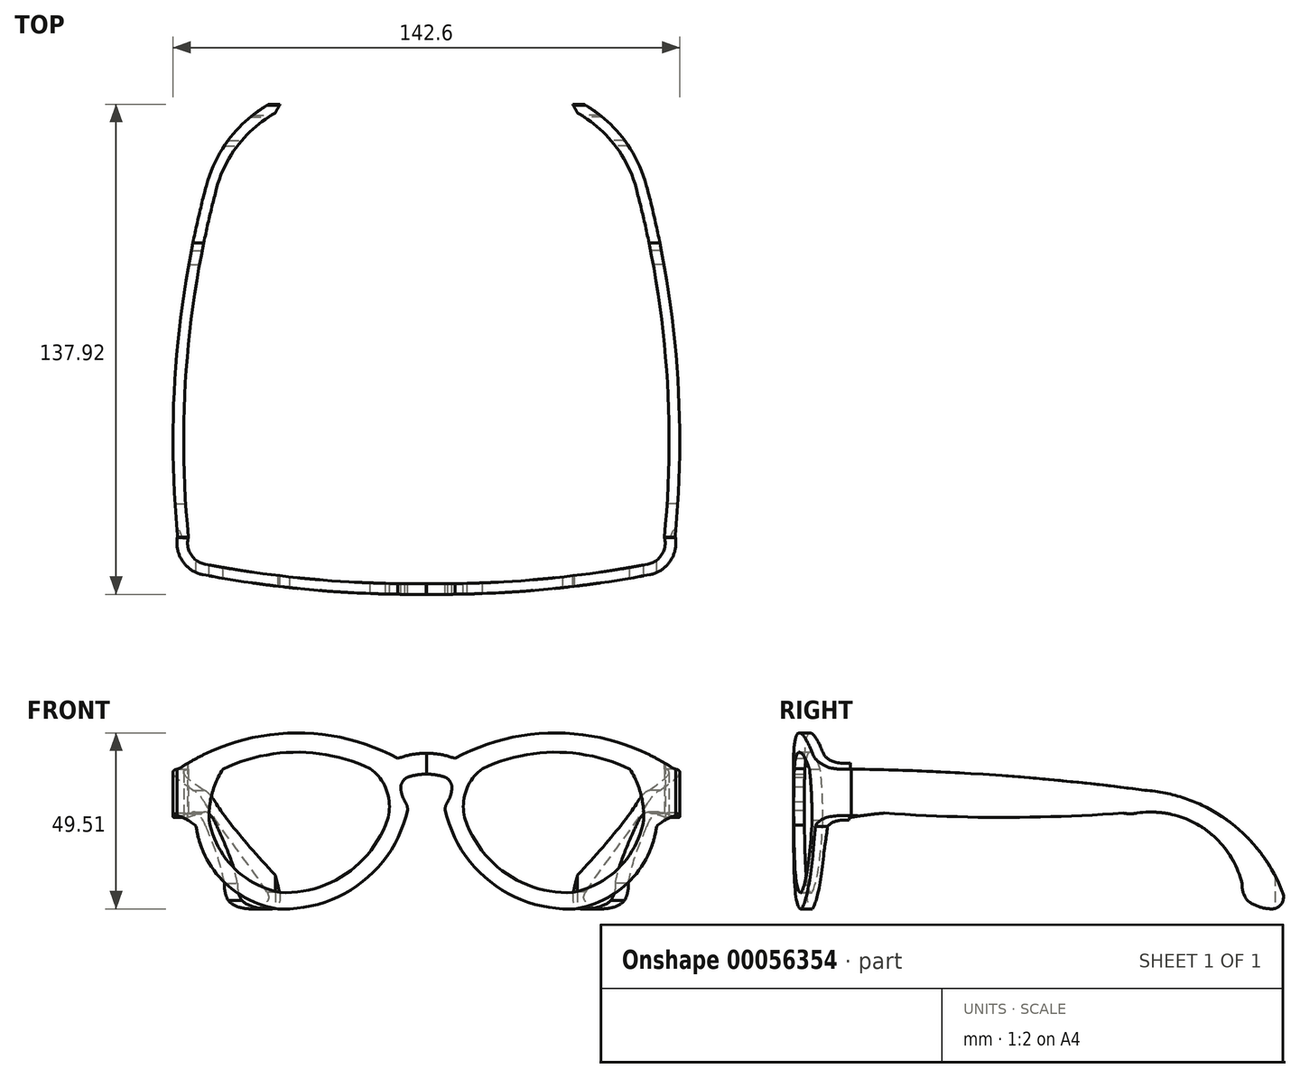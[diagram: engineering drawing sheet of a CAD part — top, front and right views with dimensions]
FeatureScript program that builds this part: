
annotation { "Feature Type Name" : "Feature", "Feature Type Description" : "" }
export const myFeature = defineFeature(function(context is Context, id is Id, definition is map)
    precondition{}
    {
        {
            var Q0;
            Q0=qCreatedBy(makeId("Top.planeOp"),FACE);
            var sketch = newSketch(context, id + "F0", { "sketchPlane" : qUnion([Q0])});
            skLineSegment(sketch, "E0.MirrorCS", {"start": v(42.53, 129.95) * mm, "end": v(40, 134.5) * mm});
            skArc(sketch, "E1.MirrorCS", {"start": v(66.96, 10.6) * mm, "mid": v(66.29, 5.73) * mm, "end": v(62.24, 2.95) * mm});
            skArc(sketch, "E2.MirrorCS", {"start": v(42.53, 129.95) * mm, "mid": v(52.96, 120.97) * mm, "end": v(59.06, 108.64) * mm});
            skArc(sketch, "E3.MirrorCS", {"start": v(62.8, 0) * mm, "mid": v(31.53, -4.3) * mm, "end": v(0, -5.5) * mm});
            skArc(sketch, "E4.MirrorCS", {"start": v(70, 10.8) * mm, "mid": v(68.67, 3.89) * mm, "end": v(62.8, 0) * mm});
            skArc(sketch, "E5.MirrorCS", {"start": v(61.96, 109.4) * mm, "mid": v(70.37, 60.47) * mm, "end": v(70, 10.8) * mm});
            skArc(sketch, "E6.MirrorCS", {"start": v(59.06, 108.64) * mm, "mid": v(67.4, 59.97) * mm, "end": v(66.96, 10.6) * mm});
            skArc(sketch, "E7.MirrorCS", {"start": v(40, 134.5) * mm, "mid": v(53.92, 124.52) * mm, "end": v(61.96, 109.4) * mm});
            skArc(sketch, "E8.MirrorCS", {"start": v(62.24, 2.95) * mm, "mid": v(31.27, -1.32) * mm, "end": v(0.04, -2.5) * mm});
            skLineSegment(sketch, "E9", {"start": v(0, -5.5) * mm, "end": v(0.04, -2.5) * mm});
            skSolve(sketch);
        }
        {
            var Q0;
            Q0=makeQuery(id+"F0.imprint","IMPRINT",FACE,{"disambiguationData":[TD([[makeQuery(id+"F0.imprint","IMPRINT",EDGE,{"derivedFrom":sQuery(id+"F0.wireOp",EDGE,"E0.MirrorCS")}),-1.0]])]});
            extrude(context, id + "F1", {"entities" : qUnion([Q0]), "depth" : 50 * mm});
        }
        {
            var Q0;
            Q0=qCreatedBy(makeId("Front.planeOp"),FACE);
            var sketch = newSketch(context, id + "F2", { "sketchPlane" : qUnion([Q0])});
            skArc(sketch, "E10", {"start": v(8, 42.31) * mm, "mid": v(4.07, 43.43) * mm, "end": v(0, 43.8) * mm});
            skArc(sketch, "E11", {"start": v(68.62, 40.04) * mm, "mid": v(38.62, 49.47) * mm, "end": v(8, 42.31) * mm});
            skArc(sketch, "E12", {"start": v(68.62, 40.04) * mm, "mid": v(70.06, 39.33) * mm, "end": v(71.62, 38.97) * mm});
            skArc(sketch, "E13", {"start": v(71.5, 26.56) * mm, "mid": v(67.9, 25.38) * mm, "end": v(64.79, 23.21) * mm});
            skArc(sketch, "E14", {"start": v(41.66, 0) * mm, "mid": v(57.1, 7.74) * mm, "end": v(64.79, 23.21) * mm});
            skArc(sketch, "E15", {"start": v(5.3, 27.81) * mm, "mid": v(18.42, 7.3) * mm, "end": v(41.66, 0) * mm});
            skArc(sketch, "E16", {"start": v(7.2, 34.4) * mm, "mid": v(6.58, 35.97) * mm, "end": v(5.3, 37.07) * mm});
            skArc(sketch, "E17", {"start": v(5.3, 37.07) * mm, "mid": v(2.68, 37.68) * mm, "end": v(0, 37.94) * mm});
            skArc(sketch, "E18", {"start": v(6.06, 30.22) * mm, "mid": v(6.9, 32.24) * mm, "end": v(7.2, 34.4) * mm});
            skArc(sketch, "E19", {"start": v(6.06, 30.22) * mm, "mid": v(5.48, 29.08) * mm, "end": v(5.3, 27.81) * mm});
            skArc(sketch, "E20", {"start": v(57.23, 39.31) * mm, "mid": v(36.51, 44.1) * mm, "end": v(15.75, 39.48) * mm});
            skArc(sketch, "E21", {"start": v(15.75, 39.48) * mm, "mid": v(10.84, 32.26) * mm, "end": v(11.52, 23.56) * mm});
            skArc(sketch, "E22", {"start": v(11.52, 23.56) * mm, "mid": v(23.33, 9.38) * mm, "end": v(41.15, 4.6) * mm});
            skArc(sketch, "E23", {"start": v(41.15, 4.6) * mm, "mid": v(54.3, 11.65) * mm, "end": v(61.13, 24.92) * mm});
            skArc(sketch, "E24", {"start": v(61.13, 24.92) * mm, "mid": v(60.33, 32.43) * mm, "end": v(57.23, 39.31) * mm});
            skLineSegment(sketch, "E25", {"start": v(0, 43.8) * mm, "end": v(0, 52.1) * mm});
            skLineSegment(sketch, "E26", {"start": v(0, 52.1) * mm, "end": v(72.74, 52.1) * mm});
            skLineSegment(sketch, "E27", {"start": v(72.74, 52.1) * mm, "end": v(71.62, 38.97) * mm});
            skLineSegment(sketch, "E28", {"start": v(0, 37.94) * mm, "end": v(0, 0) * mm});
            skLineSegment(sketch, "E29", {"start": v(0, 0) * mm, "end": v(72.57, 0) * mm});
            skLineSegment(sketch, "E30", {"start": v(72.57, 0) * mm, "end": v(71.5, 26.56) * mm});
            skSolve(sketch);
        }
        {
            var Q0;
            Q0 = qSketchRegion(id + "F2", true);
            extrude(context, id + "F3", {"entities" : qUnion([Q0]), "operationType" : NewBodyOperationType.REMOVE, "endBound" : BoundingType.SYMMETRIC, "depth" : 25 * mm});
        }
        {
            var Q0;
            Q0=qCreatedBy(makeId("Right.planeOp"),FACE);
            var sketch = newSketch(context, id + "F4", { "sketchPlane" : qUnion([Q0])});
            skArc(sketch, "E31", {"start": v(93.32, 33.4) * mm, "mid": v(52, 37.59) * mm, "end": v(10.5, 39.33) * mm});
            skArc(sketch, "E32", {"start": v(132.08, 4.75) * mm, "mid": v(116.88, 24.72) * mm, "end": v(93.32, 33.4) * mm});
            skArc(sketch, "E33", {"start": v(128.8, 0) * mm, "mid": v(131.81, 1.43) * mm, "end": v(132.08, 4.75) * mm});
            skArc(sketch, "E34", {"start": v(122.25, 2.33) * mm, "mid": v(125.34, 0.65) * mm, "end": v(128.8, 0) * mm});
            skArc(sketch, "E35", {"start": v(120.69, 7.17) * mm, "mid": v(121.05, 4.61) * mm, "end": v(122.25, 2.33) * mm});
            skArc(sketch, "E36", {"start": v(120.69, 7.17) * mm, "mid": v(109.76, 22.77) * mm, "end": v(91.17, 26.96) * mm});
            skArc(sketch, "E37", {"start": v(87.27, 26.96) * mm, "mid": v(89.22, 26.75) * mm, "end": v(91.17, 26.96) * mm});
            skArc(sketch, "E38", {"start": v(20.03, 26.96) * mm, "mid": v(53.65, 25.74) * mm, "end": v(87.27, 26.96) * mm});
            skArc(sketch, "E39", {"start": v(20.03, 26.96) * mm, "mid": v(15.1, 26.42) * mm, "end": v(10.2, 25.68) * mm});
            skLineSegment(sketch, "E40", {"start": v(10.5, 39.33) * mm, "end": v(10.2, 52.45) * mm});
            skLineSegment(sketch, "E41", {"start": v(10.2, 52.45) * mm, "end": v(139.62, 52.45) * mm});
            skLineSegment(sketch, "E42", {"start": v(139.62, 52.45) * mm, "end": v(139.62, -6.78) * mm});
            skLineSegment(sketch, "E43", {"start": v(139.62, -6.78) * mm, "end": v(8.07, -4.79) * mm});
            skLineSegment(sketch, "E44", {"start": v(8.07, -4.79) * mm, "end": v(10.2, 25.68) * mm});
            skSolve(sketch);
        }
        {
            var Q0;
            Q0 = qSketchRegion(id + "F4", true);
            extrude(context, id + "F5", {"entities" : qUnion([Q0]), "operationType" : NewBodyOperationType.REMOVE, "depth" : 120.72 * mm});
        }
        {
            var Q0;
            Q0=makeQuery(id+"F1.opExtrude","SWEPT_BODY",BODY,{"disambiguationData":[OSD([sQuery(id+"F0.wireOp",EDGE,"E0.MirrorCS"),sQuery(id+"F0.wireOp",EDGE,"E1.MirrorCS"),sQuery(id+"F0.wireOp",EDGE,"E2.MirrorCS"),sQuery(id+"F0.wireOp",EDGE,"E3.MirrorCS"),sQuery(id+"F0.wireOp",EDGE,"E4.MirrorCS"),sQuery(id+"F0.wireOp",EDGE,"E5.MirrorCS"),sQuery(id+"F0.wireOp",EDGE,"E6.MirrorCS"),sQuery(id+"F0.wireOp",EDGE,"E7.MirrorCS"),sQuery(id+"F0.wireOp",EDGE,"E8.MirrorCS"),sQuery(id+"F0.wireOp",EDGE,"E9")])]});
            var Q1;
            Q1=qCreatedBy(makeId("Right.planeOp"),FACE);
            mirror(context, id + "F6", {"entities" : qUnion([Q0]), "mirrorPlane" : qUnion([Q1])});
        }
    });
